# Revit family: Door_Operator-Sliding_Door-Ditec-Civik-Glass_Wing_and_Technical_Connection-2_Wings
name_source: partatom
category: Doors
revit_build: Autodesk Revit 2014 (Build: 20130308_1515(x64)
units: mm (PartAtom-declared; Revit-internal decimal feet)

## types (1)
- Door_Operator-Sliding_Door-Ditec-Civik-Glass_Wing_and_Technical_Connection-2_Wings
    Antipanic system = CIVIK LA
    BIMobject category = Sliding
    Closing speed = 0.4 m/s
    Control panel = EL06A (built in)
    Design country = Italy
    Duty class = 4 - heavy duty
    Edition number = 1
    Function = Interior
    Height = 2000 mm  [stored 6.56168 ft]
    IFC Classification = Door
    Installation instructions = http://ftp.ditec.it
    Manufacturer country = Italy
    Manufacturer name = Entrematic
    Masterformat 2014 Code = 08 13 73
    Masterformat 2014 Description = Sliding Metal Doors
    Material main = Aluminium
    Material secondary = Glass
    Maximum capacity = 80 kg
    NBS Reference Code = 25-30-20-77
    NBS Reference Description = Sliding Doorset Systems
    Nominal height = 75
    Nominal width = 3300
    OmniClass Code = 23-17 11 13 19
    OmniClass Description = Sliding Metal Doors
    Opening speed = 0.8 m/s
    Operating temperature = -20°C / +55°C
    Operator Length = 2700 mm  [stored 8.85827 ft]
    Operator Material = Aluminum
    Panel Material = Glass
    Power input = 0.2 A
    Power supply = 230 V AC / 50-60 Hz
    Product Guid = 023af41f-6f63-4778-8830-4f045142fb66
    Product SKU = dit-cvk
    Product data url = http://bimobject.com
    Product dimensions (mm) = 75 x130 x L
    Product family = Automatic Doors
    Product group = Sliding Automatic Doors
    Product url = http://www.ditecentrematic.com
    Protection rating = IP 20
    QR code = http://bimobject.com
    Rough Height = 2000 mm  [stored 6.56168 ft]
    Rough Width = 1200 mm
    S = 50 mm  [stored 0.164042 ft]
    Special uses = disabled use
    Stroke control = encoder
    Torque/Thrust = 30 N
    UNSPSC Code = 301715
    URL = http://www.ditecentrematic.com
    Uniclass 1.4 Code = JL20
    Uniclass 1.4 Description = Doors
    Uniclass 2.0 Code = SS-25-30-20-77
    Uniclass 2.0 Description = Sliding Doorset Systems
    Uniclass 2015 Code = Ss_25_30_20_77
    Uniclass 2015 Name = Sliding doorset systems
    Uniformat II Code = B2030
    Uniformat II Description = Exterior Doors
    Wall Closure = By host
    Weight Net (Kg) = 0
    Width = 1300 mm  [stored 4.26509 ft]

note: [stored X ft] marks values corroborated as IEEE doubles in the binary element streams (Revit-internal decimal feet)

## geometry (parser evidence)
native form markers: Blend x2, Sweep x8
no freeform markers — native parametric forms only
